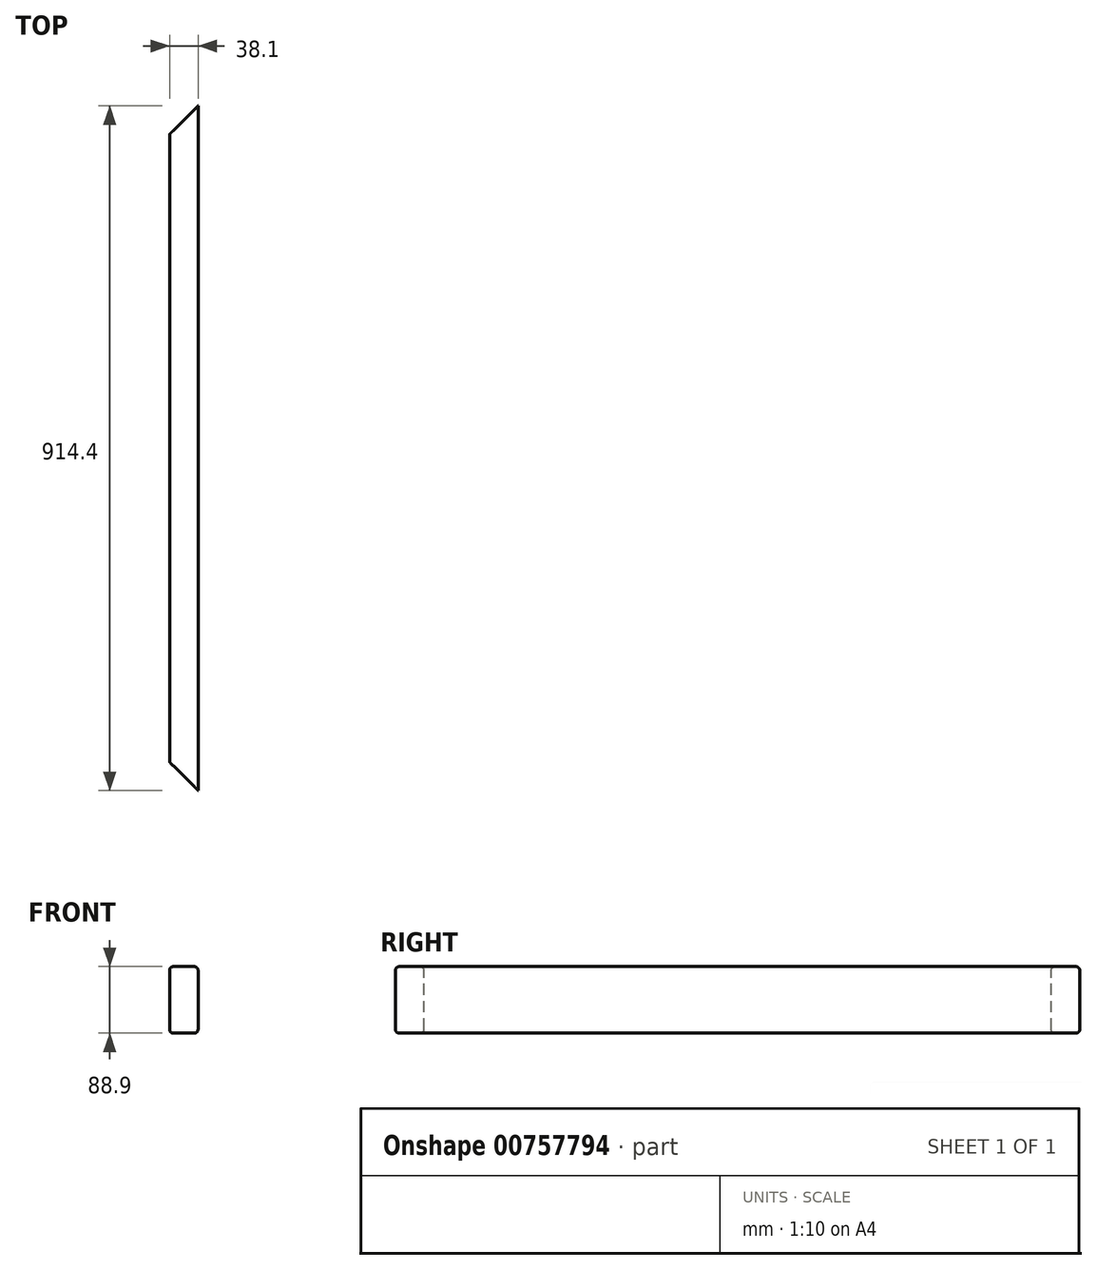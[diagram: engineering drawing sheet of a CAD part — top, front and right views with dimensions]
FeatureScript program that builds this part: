
annotation { "Feature Type Name" : "Feature", "Feature Type Description" : "" }
export const myFeature = defineFeature(function(context is Context, id is Id, definition is map)
    precondition{}
    {
        {
            var Q0;
            Q0=qCreatedBy(makeId("Front.planeOp"),FACE);
            var sketch = newSketch(context, id + "F0", { "sketchPlane" : qUnion([Q0])});
            skLineSegment(sketch, "E0.bottom", {"start": v(-23.4, 47.05) * mm, "end": v(14.7, 47.05) * mm});
            skLineSegment(sketch, "E0.top", {"start": v(-23.4, -41.85) * mm, "end": v(14.7, -41.85) * mm});
            skLineSegment(sketch, "E0.left", {"start": v(-23.4, 47.05) * mm, "end": v(-23.4, -41.85) * mm});
            skLineSegment(sketch, "E0.right", {"start": v(14.7, 47.05) * mm, "end": v(14.7, -41.85) * mm});
            skSolve(sketch);
        }
        {
            var Q0;
            Q0=makeQuery(id+"F0.imprint","IMPRINT",FACE,{"disambiguationData":[TD([[makeQuery(id+"F0.imprint","IMPRINT",EDGE,{"derivedFrom":sQuery(id+"F0.wireOp",EDGE,"E0.bottom")}),-1.0]])]});
            extrude(context, id + "F1", {"entities" : qUnion([Q0]), "depth" : 914.4 * mm, "offsetDistance" : 25.4 * mm});
        }
        {
            var Q0;
            Q0=makeQuery(id+"F1.opExtrude","SWEPT_FACE",FACE,{"disambiguationData":[OSD([sQuery(id+"F0.wireOp",EDGE,"E0.bottom")])]});
            var sketch = newSketch(context, id + "F2", { "sketchPlane" : qUnion([Q0])});
            skLineSegment(sketch, "E1", {"start": v(14.7, 0) * mm, "end": v(-23.4, -38.1) * mm});
            skLineSegment(sketch, "E2", {"start": v(-23.4, -38.1) * mm, "end": v(-23.4, 0) * mm});
            skLineSegment(sketch, "E3", {"start": v(-23.4, 0) * mm, "end": v(14.7, 0) * mm});
            skLineSegment(sketch, "E4", {"start": v(14.7, -914.4) * mm, "end": v(-23.4, -876.3) * mm});
            skLineSegment(sketch, "E5", {"start": v(-23.4, -876.3) * mm, "end": v(-23.4, -914.4) * mm});
            skLineSegment(sketch, "E6", {"start": v(-23.4, -914.4) * mm, "end": v(14.7, -914.4) * mm});
            skSolve(sketch);
        }
        {
            var Q0;
            Q0=makeQuery(id+"F2.imprint","IMPRINT",FACE,{"disambiguationData":[TD([[makeQuery(id+"F2.imprint","IMPRINT",EDGE,{"derivedFrom":sQuery(id+"F2.wireOp",EDGE,"E4")}),1.0]])]});
            var Q1;
            Q1=makeQuery(id+"F2.imprint","IMPRINT",FACE,{"disambiguationData":[TD([[makeQuery(id+"F2.imprint","IMPRINT",EDGE,{"derivedFrom":sQuery(id+"F2.wireOp",EDGE,"E1")}),-1.0]])]});
            extrude(context, id + "F3", {"entities" : qUnion([Q0, Q1]), "operationType" : NewBodyOperationType.REMOVE, "oppositeDirection" : true, "depth" : 88.9 * mm, "offsetDistance" : 25.4 * mm});
        }
        {
            var Q0;
            Q0=makeQuery(id+"F1.opExtrude","SWEPT_EDGE",EDGE,{"disambiguationData":[OSD([sQuery(id+"F0.wireOp",EDGE,"E0.bottom"),sQuery(id+"F0.wireOp",EDGE,"E0.left")])]});
            var Q1;
            Q1=makeQuery(id+"F1.opExtrude","SWEPT_EDGE",EDGE,{"disambiguationData":[OSD([sQuery(id+"F0.wireOp",EDGE,"E0.bottom"),sQuery(id+"F0.wireOp",EDGE,"E0.right")])]});
            var Q2;
            Q2=makeQuery(id+"F1.opExtrude","SWEPT_EDGE",EDGE,{"disambiguationData":[OSD([sQuery(id+"F0.wireOp",EDGE,"E0.top"),sQuery(id+"F0.wireOp",EDGE,"E0.left")])]});
            var Q3;
            Q3=makeQuery(id+"F1.opExtrude","SWEPT_EDGE",EDGE,{"disambiguationData":[OSD([sQuery(id+"F0.wireOp",EDGE,"E0.top"),sQuery(id+"F0.wireOp",EDGE,"E0.right")])]});
            fillet(context, id + "F4", {"entities" : qUnion([Q0, Q1, Q2, Q3]), "radius" : 5.08 * mm, "tangentPropagation" : true, "allowEdgeOverflow" : false});
        }
    });
